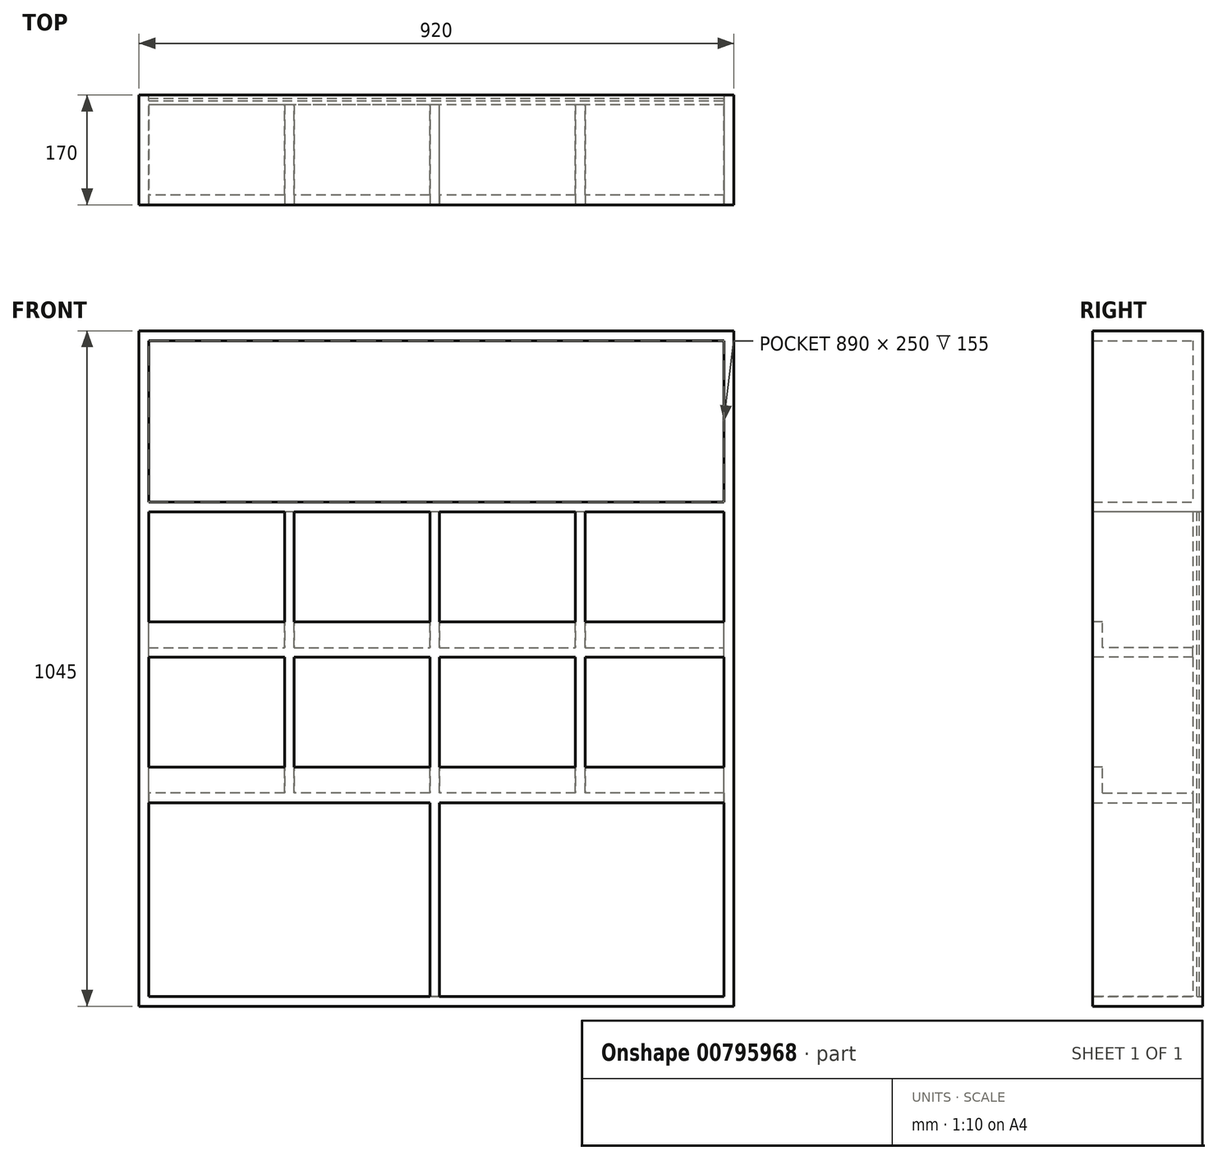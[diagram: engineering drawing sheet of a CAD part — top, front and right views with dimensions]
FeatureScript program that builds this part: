
annotation { "Feature Type Name" : "Feature", "Feature Type Description" : "" }
export const myFeature = defineFeature(function(context is Context, id is Id, definition is map)
    precondition{}
    {
        {
            var Q0;
            Q0=qCreatedBy(makeId("Front.planeOp"),FACE);
            var sketch = newSketch(context, id + "F0", { "sketchPlane" : qUnion([Q0])});
            skLineSegment(sketch, "E0.bottom", {"start": v(-460, 0) * mm, "end": v(460, 0) * mm});
            skLineSegment(sketch, "E0.top", {"start": v(-460, 1045) * mm, "end": v(460, 1045) * mm});
            skLineSegment(sketch, "E0.left", {"start": v(-460, 0) * mm, "end": v(-460, 1045) * mm});
            skLineSegment(sketch, "E0.right", {"start": v(460, 0) * mm, "end": v(460, 1045) * mm});
            skSolve(sketch);
        }
        {
            var Q0;
            Q0 = qSketchRegion(id + "F0", true);
            extrude(context, id + "F1", {"entities" : qUnion([Q0]), "depth" : 170 * mm, "offsetDistance" : 25 * mm});
        }
        {
            var Q0;
            Q0=makeQuery(id+"F1.opExtrude","CAP_FACE",FACE,{"disambiguationData":[OSD([sQuery(id+"F0.wireOp",EDGE,"E0.bottom"),sQuery(id+"F0.wireOp",EDGE,"E0.top"),sQuery(id+"F0.wireOp",EDGE,"E0.left"),sQuery(id+"F0.wireOp",EDGE,"E0.right")])],"isStart":false});
            var Q1;
            Q1=makeQuery(id+"F1.opExtrude","CAP_FACE",FACE,{"disambiguationData":[OSD([sQuery(id+"F0.wireOp",EDGE,"E0.bottom"),sQuery(id+"F0.wireOp",EDGE,"E0.top"),sQuery(id+"F0.wireOp",EDGE,"E0.left"),sQuery(id+"F0.wireOp",EDGE,"E0.right")])],"isStart":true});
            shell(context, id + "F2", {"entities" : qUnion([Q0, Q1]), "thickness" : 15 * mm});
        }
        {
            var Q0;
            Q0=makeQuery(id+"F1.opExtrude","CAP_FACE",FACE,{"disambiguationData":[OSD([sQuery(id+"F0.wireOp",EDGE,"E0.bottom"),sQuery(id+"F0.wireOp",EDGE,"E0.top"),sQuery(id+"F0.wireOp",EDGE,"E0.left"),sQuery(id+"F0.wireOp",EDGE,"E0.right")])],"isStart":true});
            var sketch = newSketch(context, id + "F3", { "sketchPlane" : qUnion([Q0])});
            skLineSegment(sketch, "E1.bottom", {"start": v(-460, 1045) * mm, "end": v(460, 1045) * mm});
            skLineSegment(sketch, "E1.top", {"start": v(-460, 765) * mm, "end": v(460, 765) * mm});
            skLineSegment(sketch, "E1.left", {"start": v(-460, 1045) * mm, "end": v(-460, 765) * mm});
            skLineSegment(sketch, "E1.right", {"start": v(460, 1045) * mm, "end": v(460, 765) * mm});
            skSolve(sketch);
        }
        {
            var Q0;
            Q0 = qSketchRegion(id + "F3", true);
            extrude(context, id + "F4", {"entities" : qUnion([Q0]), "operationType" : NewBodyOperationType.ADD, "oppositeDirection" : true, "depth" : 15 * mm, "offsetDistance" : 25 * mm});
        }
        {
            var Q0;
            Q0=makeQuery(id+"F4.boolean.opBoolean","MERGE",FACE,{"derivedFrom":[makeQuery(id+"F1.opExtrude","CAP_FACE",FACE,{"disambiguationData":[OSD([sQuery(id+"F0.wireOp",EDGE,"E0.bottom"),sQuery(id+"F0.wireOp",EDGE,"E0.top"),sQuery(id+"F0.wireOp",EDGE,"E0.left"),sQuery(id+"F0.wireOp",EDGE,"E0.right")])],"isStart":true}),makeQuery(id+"F4.opExtrude","CAP_FACE",FACE,{"disambiguationData":[OSD([sQuery(id+"F3.wireOp",EDGE,"E1.bottom"),sQuery(id+"F3.wireOp",EDGE,"E1.top"),sQuery(id+"F3.wireOp",EDGE,"E1.left"),sQuery(id+"F3.wireOp",EDGE,"E1.right")])],"isStart":true})]});
            var sketch = newSketch(context, id + "F5", { "sketchPlane" : qUnion([Q0])});
            skLineSegment(sketch, "E2.bottom", {"start": v(-445, 15) * mm, "end": v(445, 15) * mm});
            skLineSegment(sketch, "E2.top", {"start": v(-445, 765) * mm, "end": v(445, 765) * mm});
            skLineSegment(sketch, "E2.left", {"start": v(-445, 15) * mm, "end": v(-445, 765) * mm});
            skLineSegment(sketch, "E2.right", {"start": v(445, 15) * mm, "end": v(445, 765) * mm});
            skSolve(sketch);
        }
        {
            var Q0;
            Q0 = qSketchRegion(id + "F5", true);
            extrude(context, id + "F6", {"entities" : qUnion([Q0]), "oppositeDirection" : true, "depth" : 4 * mm, "offsetDistance" : 25 * mm});
        }
        {
            var Q0;
            Q0=makeQuery(id+"F4.opExtrude","CAP_FACE",FACE,{"disambiguationData":[OSD([sQuery(id+"F3.wireOp",EDGE,"E1.bottom"),sQuery(id+"F3.wireOp",EDGE,"E1.top"),sQuery(id+"F3.wireOp",EDGE,"E1.left"),sQuery(id+"F3.wireOp",EDGE,"E1.right")])],"isStart":false});
            var sketch = newSketch(context, id + "F7", { "sketchPlane" : qUnion([Q0])});
            skLineSegment(sketch, "E3.0", {"start": v(445, 765) * mm, "end": v(-445, 765) * mm});
            skLineSegment(sketch, "E4.0", {"start": v(445, 780) * mm, "end": v(-445, 780) * mm});
            skLineSegment(sketch, "E5", {"start": v(-445, 780) * mm, "end": v(-445, 765) * mm});
            skLineSegment(sketch, "E6", {"start": v(445, 780) * mm, "end": v(445, 765) * mm});
            skLineSegment(sketch, "E7.0", {"start": v(445, 315) * mm, "end": v(-445, 315) * mm});
            skLineSegment(sketch, "E8.0", {"start": v(445, 330) * mm, "end": v(-445, 330) * mm});
            skLineSegment(sketch, "E9", {"start": v(-445, 330) * mm, "end": v(-445, 315) * mm});
            skLineSegment(sketch, "E10", {"start": v(445, 330) * mm, "end": v(445, 315) * mm});
            skSolve(sketch);
        }
        {
            var Q0;
            Q0 = qSketchRegion(id + "F7", true);
            var Q1;
            Q1=makeQuery(id+"F1.opExtrude","CAP_FACE",FACE,{"disambiguationData":[OSD([sQuery(id+"F0.wireOp",EDGE,"E0.bottom"),sQuery(id+"F0.wireOp",EDGE,"E0.top"),sQuery(id+"F0.wireOp",EDGE,"E0.left"),sQuery(id+"F0.wireOp",EDGE,"E0.right")])],"isStart":false});
            extrude(context, id + "F8", {"entities" : qUnion([Q0]), "operationType" : NewBodyOperationType.ADD, "endBound" : BoundingType.UP_TO_SURFACE, "depth" : 25 * mm, "endBoundEntityFace" : qUnion([Q1]), "offsetDistance" : 25 * mm});
        }
        {
            var Q0;
            {var subQ0=sQuery(id+"F0.wireOp",EDGE,"E0.right");var subQ1=sQuery(id+"F0.wireOp",EDGE,"E0.left");var subQ2=sQuery(id+"F0.wireOp",EDGE,"E0.top");var subQ3=sQuery(id+"F0.wireOp",EDGE,"E0.bottom");Q0=makeQuery(id+"F8.boolean.opBoolean","MERGE",FACE,{"derivedFrom":[makeQuery(id+"F1.opExtrude","CAP_FACE",FACE,{"disambiguationData":[OSD([subQ3,subQ2,subQ1,subQ0])],"isStart":false}),makeQuery(id+"F8.opExtrude","CAP_FACE",FACE,{"disambiguationData":[OSD([subQ3,subQ2,subQ1,subQ0]),OD(0.0)],"isStart":false}),makeQuery(id+"F8.opExtrude","CAP_FACE",FACE,{"disambiguationData":[OSD([subQ3,subQ2,subQ1,subQ0]),OD(1.0)],"isStart":false})]});}
            var sketch = newSketch(context, id + "F9", { "sketchPlane" : qUnion([Q0])});
            skLineSegment(sketch, "E11.bottom", {"start": v(-445, 555) * mm, "end": v(445, 555) * mm});
            skLineSegment(sketch, "E11.top", {"start": v(-445, 540) * mm, "end": v(445, 540) * mm});
            skLineSegment(sketch, "E11.left", {"start": v(-445, 555) * mm, "end": v(-445, 540) * mm});
            skLineSegment(sketch, "E11.right", {"start": v(445, 555) * mm, "end": v(445, 540) * mm});
            skSolve(sketch);
        }
        {
            var Q0;
            Q0 = qSketchRegion(id + "F9", true);
            var Q1;
            Q1=makeQuery(id+"F4.opExtrude","CAP_FACE",FACE,{"disambiguationData":[OSD([sQuery(id+"F3.wireOp",EDGE,"E1.bottom"),sQuery(id+"F3.wireOp",EDGE,"E1.top"),sQuery(id+"F3.wireOp",EDGE,"E1.left"),sQuery(id+"F3.wireOp",EDGE,"E1.right")])],"isStart":false});
            extrude(context, id + "F10", {"entities" : qUnion([Q0]), "operationType" : NewBodyOperationType.ADD, "endBound" : BoundingType.UP_TO_SURFACE, "oppositeDirection" : true, "depth" : 25 * mm, "endBoundEntityFace" : qUnion([Q1]), "offsetDistance" : 25 * mm});
        }
        {
            var Q0;
            {var subQ0=sQuery(id+"F0.wireOp",EDGE,"E0.right");var subQ1=sQuery(id+"F0.wireOp",EDGE,"E0.left");var subQ2=sQuery(id+"F0.wireOp",EDGE,"E0.top");var subQ3=sQuery(id+"F0.wireOp",EDGE,"E0.bottom");Q0=makeQuery(id+"F10.boolean.opBoolean","MERGE",FACE,{"derivedFrom":[makeQuery(id+"F8.boolean.opBoolean","MERGE",FACE,{"derivedFrom":[makeQuery(id+"F1.opExtrude","CAP_FACE",FACE,{"disambiguationData":[OSD([subQ3,subQ2,subQ1,subQ0])],"isStart":false}),makeQuery(id+"F8.opExtrude","CAP_FACE",FACE,{"disambiguationData":[OSD([subQ3,subQ2,subQ1,subQ0]),OD(0.0)],"isStart":false}),makeQuery(id+"F8.opExtrude","CAP_FACE",FACE,{"disambiguationData":[OSD([subQ3,subQ2,subQ1,subQ0]),OD(1.0)],"isStart":false})]}),makeQuery(id+"F10.opExtrude","CAP_FACE",FACE,{"disambiguationData":[OSD([sQuery(id+"F9.wireOp",EDGE,"E11.bottom"),sQuery(id+"F9.wireOp",EDGE,"E11.top"),sQuery(id+"F9.wireOp",EDGE,"E11.left"),sQuery(id+"F9.wireOp",EDGE,"E11.right")])],"isStart":true})]});}
            var sketch = newSketch(context, id + "F11", { "sketchPlane" : qUnion([Q0])});
            skLineSegment(sketch, "E12.bottom", {"start": v(-235, 765) * mm, "end": v(-220, 765) * mm});
            skLineSegment(sketch, "E12.top", {"start": v(-235, 330) * mm, "end": v(-220, 330) * mm});
            skLineSegment(sketch, "E12.left", {"start": v(-235, 765) * mm, "end": v(-235, 330) * mm});
            skLineSegment(sketch, "E12.right", {"start": v(-220, 765) * mm, "end": v(-220, 330) * mm});
            skLineSegment(sketch, "E13.1.0.0", {"start": v(-10, 765) * mm, "end": v(-10, 330) * mm});
            skLineSegment(sketch, "E13.1.0.1", {"start": v(5, 765) * mm, "end": v(5, 330) * mm});
            skLineSegment(sketch, "E13.1.0.2", {"start": v(-10, 765) * mm, "end": v(5, 765) * mm});
            skLineSegment(sketch, "E13.1.0.3", {"start": v(-10, 330) * mm, "end": v(5, 330) * mm});
            skLineSegment(sketch, "E13.2.0.0", {"start": v(215, 765) * mm, "end": v(215, 330) * mm});
            skLineSegment(sketch, "E13.2.0.1", {"start": v(230, 765) * mm, "end": v(230, 330) * mm});
            skLineSegment(sketch, "E13.2.0.2", {"start": v(215, 765) * mm, "end": v(230, 765) * mm});
            skLineSegment(sketch, "E13.2.0.3", {"start": v(215, 330) * mm, "end": v(230, 330) * mm});
            skLineSegment(sketch, "E13.direction1", {"start": v(-235, 330) * mm, "end": v(-10, 330) * mm, "construction": true});
            skSolve(sketch);
        }
        {
            var Q0;
            Q0 = qSketchRegion(id + "F11", true);
            var Q1;
            Q1=makeQuery(id+"F4.opExtrude","CAP_FACE",FACE,{"disambiguationData":[OSD([sQuery(id+"F3.wireOp",EDGE,"E1.bottom"),sQuery(id+"F3.wireOp",EDGE,"E1.top"),sQuery(id+"F3.wireOp",EDGE,"E1.left"),sQuery(id+"F3.wireOp",EDGE,"E1.right")])],"isStart":false});
            extrude(context, id + "F12", {"entities" : qUnion([Q0]), "operationType" : NewBodyOperationType.ADD, "endBound" : BoundingType.UP_TO_SURFACE, "oppositeDirection" : true, "depth" : 25 * mm, "endBoundEntityFace" : qUnion([Q1]), "offsetDistance" : 25 * mm});
        }
        {
            var Q0;
            {var subQ0=sQuery(id+"F0.wireOp",EDGE,"E0.right");var subQ1=sQuery(id+"F0.wireOp",EDGE,"E0.left");var subQ2=sQuery(id+"F0.wireOp",EDGE,"E0.top");var subQ3=sQuery(id+"F0.wireOp",EDGE,"E0.bottom");Q0=makeQuery(id+"F12.boolean.opBoolean","MERGE",FACE,{"derivedFrom":[makeQuery(id+"F10.boolean.opBoolean","MERGE",FACE,{"derivedFrom":[makeQuery(id+"F8.boolean.opBoolean","MERGE",FACE,{"derivedFrom":[makeQuery(id+"F1.opExtrude","CAP_FACE",FACE,{"disambiguationData":[OSD([subQ3,subQ2,subQ1,subQ0])],"isStart":false}),makeQuery(id+"F8.opExtrude","CAP_FACE",FACE,{"disambiguationData":[OSD([subQ3,subQ2,subQ1,subQ0]),OD(0.0)],"isStart":false}),makeQuery(id+"F8.opExtrude","CAP_FACE",FACE,{"disambiguationData":[OSD([subQ3,subQ2,subQ1,subQ0]),OD(1.0)],"isStart":false})]}),makeQuery(id+"F10.opExtrude","CAP_FACE",FACE,{"disambiguationData":[OSD([sQuery(id+"F9.wireOp",EDGE,"E11.bottom"),sQuery(id+"F9.wireOp",EDGE,"E11.top"),sQuery(id+"F9.wireOp",EDGE,"E11.left"),sQuery(id+"F9.wireOp",EDGE,"E11.right")])],"isStart":true})]}),makeQuery(id+"F12.opExtrude","CAP_FACE",FACE,{"disambiguationData":[OSD([sQuery(id+"F11.wireOp",EDGE,"E12.bottom"),sQuery(id+"F11.wireOp",EDGE,"E12.top"),sQuery(id+"F11.wireOp",EDGE,"E12.left"),sQuery(id+"F11.wireOp",EDGE,"E12.right")])],"isStart":true}),makeQuery(id+"F12.opExtrude","CAP_FACE",FACE,{"disambiguationData":[OSD([sQuery(id+"F11.wireOp",EDGE,"E13.1.0.0"),sQuery(id+"F11.wireOp",EDGE,"E13.1.0.1"),sQuery(id+"F11.wireOp",EDGE,"E13.1.0.2"),sQuery(id+"F11.wireOp",EDGE,"E13.1.0.3")])],"isStart":true}),makeQuery(id+"F12.opExtrude","CAP_FACE",FACE,{"disambiguationData":[OSD([sQuery(id+"F11.wireOp",EDGE,"E13.2.0.0"),sQuery(id+"F11.wireOp",EDGE,"E13.2.0.1"),sQuery(id+"F11.wireOp",EDGE,"E13.2.0.2"),sQuery(id+"F11.wireOp",EDGE,"E13.2.0.3")])],"isStart":true})]});}
            var sketch = newSketch(context, id + "F13", { "sketchPlane" : qUnion([Q0])});
            skLineSegment(sketch, "E14.bottom", {"start": v(-445, 330) * mm, "end": v(445, 330) * mm});
            skLineSegment(sketch, "E14.top", {"start": v(-445, 370) * mm, "end": v(445, 370) * mm});
            skLineSegment(sketch, "E14.left", {"start": v(-445, 330) * mm, "end": v(-445, 370) * mm});
            skLineSegment(sketch, "E14.right", {"start": v(445, 330) * mm, "end": v(445, 370) * mm});
            skLineSegment(sketch, "E15.bottom", {"start": v(-445, 555) * mm, "end": v(445, 555) * mm});
            skLineSegment(sketch, "E15.top", {"start": v(-445, 595) * mm, "end": v(445, 595) * mm});
            skLineSegment(sketch, "E15.left", {"start": v(-445, 555) * mm, "end": v(-445, 595) * mm});
            skLineSegment(sketch, "E15.right", {"start": v(445, 555) * mm, "end": v(445, 595) * mm});
            skSolve(sketch);
        }
        {
            var Q0;
            Q0 = qSketchRegion(id + "F13", true);
            extrude(context, id + "F14", {"entities" : qUnion([Q0]), "operationType" : NewBodyOperationType.ADD, "oppositeDirection" : true, "depth" : 15 * mm, "offsetDistance" : 25 * mm});
        }
        {
            var Q0;
            {var subQ0=sQuery(id+"F0.wireOp",EDGE,"E0.right");var subQ1=sQuery(id+"F0.wireOp",EDGE,"E0.left");var subQ2=sQuery(id+"F0.wireOp",EDGE,"E0.top");var subQ3=sQuery(id+"F0.wireOp",EDGE,"E0.bottom");Q0=makeQuery(id+"F14.boolean.opBoolean","MERGE",FACE,{"derivedFrom":[makeQuery(id+"F12.boolean.opBoolean","MERGE",FACE,{"derivedFrom":[makeQuery(id+"F10.boolean.opBoolean","MERGE",FACE,{"derivedFrom":[makeQuery(id+"F8.boolean.opBoolean","MERGE",FACE,{"derivedFrom":[makeQuery(id+"F1.opExtrude","CAP_FACE",FACE,{"disambiguationData":[OSD([subQ3,subQ2,subQ1,subQ0])],"isStart":false}),makeQuery(id+"F8.opExtrude","CAP_FACE",FACE,{"disambiguationData":[OSD([subQ3,subQ2,subQ1,subQ0]),OD(0.0)],"isStart":false}),makeQuery(id+"F8.opExtrude","CAP_FACE",FACE,{"disambiguationData":[OSD([subQ3,subQ2,subQ1,subQ0]),OD(1.0)],"isStart":false})]}),makeQuery(id+"F10.opExtrude","CAP_FACE",FACE,{"disambiguationData":[OSD([sQuery(id+"F9.wireOp",EDGE,"E11.bottom"),sQuery(id+"F9.wireOp",EDGE,"E11.top"),sQuery(id+"F9.wireOp",EDGE,"E11.left"),sQuery(id+"F9.wireOp",EDGE,"E11.right")])],"isStart":true})]}),makeQuery(id+"F12.opExtrude","CAP_FACE",FACE,{"disambiguationData":[OSD([sQuery(id+"F11.wireOp",EDGE,"E12.bottom"),sQuery(id+"F11.wireOp",EDGE,"E12.top"),sQuery(id+"F11.wireOp",EDGE,"E12.left"),sQuery(id+"F11.wireOp",EDGE,"E12.right")])],"isStart":true}),makeQuery(id+"F12.opExtrude","CAP_FACE",FACE,{"disambiguationData":[OSD([sQuery(id+"F11.wireOp",EDGE,"E13.1.0.0"),sQuery(id+"F11.wireOp",EDGE,"E13.1.0.1"),sQuery(id+"F11.wireOp",EDGE,"E13.1.0.2"),sQuery(id+"F11.wireOp",EDGE,"E13.1.0.3")])],"isStart":true}),makeQuery(id+"F12.opExtrude","CAP_FACE",FACE,{"disambiguationData":[OSD([sQuery(id+"F11.wireOp",EDGE,"E13.2.0.0"),sQuery(id+"F11.wireOp",EDGE,"E13.2.0.1"),sQuery(id+"F11.wireOp",EDGE,"E13.2.0.2"),sQuery(id+"F11.wireOp",EDGE,"E13.2.0.3")])],"isStart":true})]}),makeQuery(id+"F14.opExtrude","CAP_FACE",FACE,{"disambiguationData":[OSD([sQuery(id+"F13.wireOp",EDGE,"E14.bottom"),sQuery(id+"F13.wireOp",EDGE,"E14.top"),sQuery(id+"F13.wireOp",EDGE,"E14.left"),sQuery(id+"F13.wireOp",EDGE,"E14.right")])],"isStart":true}),makeQuery(id+"F14.opExtrude","CAP_FACE",FACE,{"disambiguationData":[OSD([sQuery(id+"F13.wireOp",EDGE,"E15.bottom"),sQuery(id+"F13.wireOp",EDGE,"E15.top"),sQuery(id+"F13.wireOp",EDGE,"E15.left"),sQuery(id+"F13.wireOp",EDGE,"E15.right")])],"isStart":true})]});}
            var sketch = newSketch(context, id + "F15", { "sketchPlane" : qUnion([Q0])});
            skLineSegment(sketch, "E16.bottom", {"start": v(-10, 370) * mm, "end": v(5, 370) * mm});
            skLineSegment(sketch, "E16.top", {"start": v(-10, 0) * mm, "end": v(5, 0) * mm});
            skLineSegment(sketch, "E16.left", {"start": v(-10, 370) * mm, "end": v(-10, 0) * mm});
            skLineSegment(sketch, "E16.right", {"start": v(5, 370) * mm, "end": v(5, 0) * mm});
            skSolve(sketch);
        }
        {
            var Q0;
            Q0 = qSketchRegion(id + "F15", true);
            var Q1;
            Q1=makeQuery(id+"F4.opExtrude","CAP_FACE",FACE,{"disambiguationData":[OSD([sQuery(id+"F3.wireOp",EDGE,"E1.bottom"),sQuery(id+"F3.wireOp",EDGE,"E1.top"),sQuery(id+"F3.wireOp",EDGE,"E1.left"),sQuery(id+"F3.wireOp",EDGE,"E1.right")])],"isStart":false});
            extrude(context, id + "F16", {"entities" : qUnion([Q0]), "operationType" : NewBodyOperationType.ADD, "endBound" : BoundingType.UP_TO_SURFACE, "oppositeDirection" : true, "depth" : 25 * mm, "endBoundEntityFace" : qUnion([Q1]), "offsetDistance" : 25 * mm});
        }
        {
            var Q0;
            Q0=makeQuery(id+"F6.opExtrude","SWEPT_BODY",BODY,{"disambiguationData":[OSD([sQuery(id+"F5.wireOp",EDGE,"E2.bottom"),sQuery(id+"F5.wireOp",EDGE,"E2.top"),sQuery(id+"F5.wireOp",EDGE,"E2.left"),sQuery(id+"F5.wireOp",EDGE,"E2.right")])]});
            var Q1;
            {var subQ0=sQuery(id+"F0.wireOp",EDGE,"E0.left");var subQ1=sQuery(id+"F0.wireOp",EDGE,"E0.bottom");Q1=makeQuery(id+"F2.opShell","OFFSET_VERTEX",VERTEX,{"disambiguationData":[OSD([subQ1,subQ0]),TDD([makeQuery(id+"F1.opExtrude","CAP_VERTEX",VERTEX,{"disambiguationData":[OSD([subQ1,subQ0])],"isStart":true})])]});}
            var Q2;
            Q2=makeQuery(id+"F6.opExtrude","CAP_FACE",FACE,{"disambiguationData":[OSD([sQuery(id+"F5.wireOp",EDGE,"E2.bottom"),sQuery(id+"F5.wireOp",EDGE,"E2.top"),sQuery(id+"F5.wireOp",EDGE,"E2.left"),sQuery(id+"F5.wireOp",EDGE,"E2.right")])],"isStart":true});
            transform(context, id + "F17", {"entities" : qUnion([Q0]), "transformType" : TransformType.TRANSLATION_DISTANCE, "transformDirection" : qUnion([Q2]), "distance" : 5 * mm, "oppositeDirection" : true, "makeCopy" : false});
        }
    });
